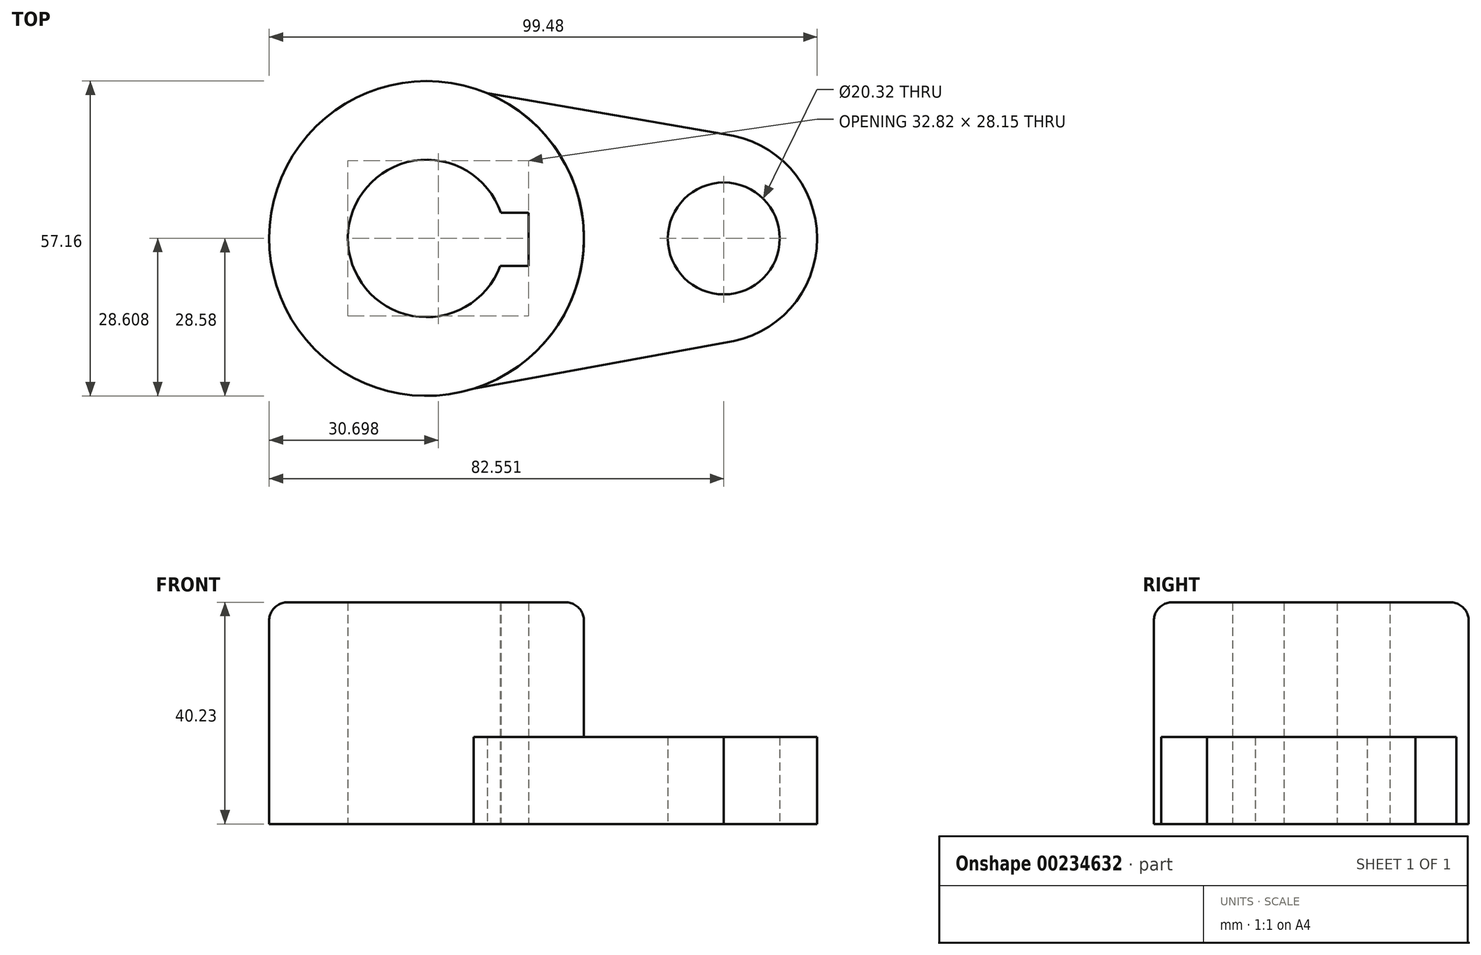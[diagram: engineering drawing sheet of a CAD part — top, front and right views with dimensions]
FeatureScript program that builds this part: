
annotation { "Feature Type Name" : "Feature", "Feature Type Description" : "" }
export const myFeature = defineFeature(function(context is Context, id is Id, definition is map)
    precondition{}
    {
        {
            var Q0;
            Q0=qCreatedBy(makeId("Top.planeOp"),FACE);
            var sketch = newSketch(context, id + "F0", { "sketchPlane" : qUnion([Q0])});
            skCircle(sketch, "E0", {"center": v(-22.53, 0) * mm, "radius": 28.58 * mm});
            skCircle(sketch, "E1", {"center": v(31.44, 0) * mm, "radius": 10.16 * mm});
            skArc(sketch, "E2", {"start": v(-9.03, 4.67) * mm, "mid": v(-36.82, 0.16) * mm, "end": v(-9.14, -4.98) * mm});
            skLineSegment(sketch, "E3.bottom", {"start": v(-9.03, 4.67) * mm, "end": v(-4, 4.67) * mm});
            skLineSegment(sketch, "E3.top", {"start": v(-9.14, -4.98) * mm, "end": v(-4, -4.98) * mm});
            skLineSegment(sketch, "E3.right", {"start": v(-4, 4.67) * mm, "end": v(-4, -4.98) * mm});
            skArc(sketch, "E4", {"start": v(31.44, -18.93) * mm, "mid": v(48.37, 0) * mm, "end": v(31.44, 18.93) * mm});
            skLineSegment(sketch, "E5", {"start": v(31.44, -18.93) * mm, "end": v(-14, -27.27) * mm});
            skLineSegment(sketch, "E6", {"start": v(31.44, 18.93) * mm, "end": v(-11.53, 26.37) * mm});
            skSolve(sketch);
        }
        {
            var Q0;
            Q0=makeQuery(id+"F0.imprint","IMPRINT",FACE,{"disambiguationData":[TD([[makeQuery(id+"F0.imprint","IMPRINT",EDGE,{"derivedFrom":sQuery(id+"F0.wireOp",EDGE,"E2")}),-1.0]])]});
            extrude(context, id + "F1", {"entities" : qUnion([Q0]), "depth" : 40.23 * mm});
        }
        {
            var Q0;
            Q0=makeQuery(id+"F0.imprint","IMPRINT",FACE,{"disambiguationData":[TD([[makeQuery(id+"F0.imprint","IMPRINT",EDGE,{"derivedFrom":sQuery(id+"F0.wireOp",EDGE,"E1")}),-1.0]])]});
            extrude(context, id + "F2", {"entities" : qUnion([Q0]), "operationType" : NewBodyOperationType.ADD, "depth" : 15.77 * mm});
        }
        {
            var Q0;
            Q0=makeQuery(id+"F1.opExtrude","CAP_EDGE",EDGE,{"disambiguationData":[OSD([sQuery(id+"F0.wireOp",EDGE,"E0")])],"isStart":false});
            fillet(context, id + "F3", {"entities" : qUnion([Q0]), "radius" : 3.3 * mm, "tangentPropagation" : true, "allowEdgeOverflow" : false});
        }
    });
